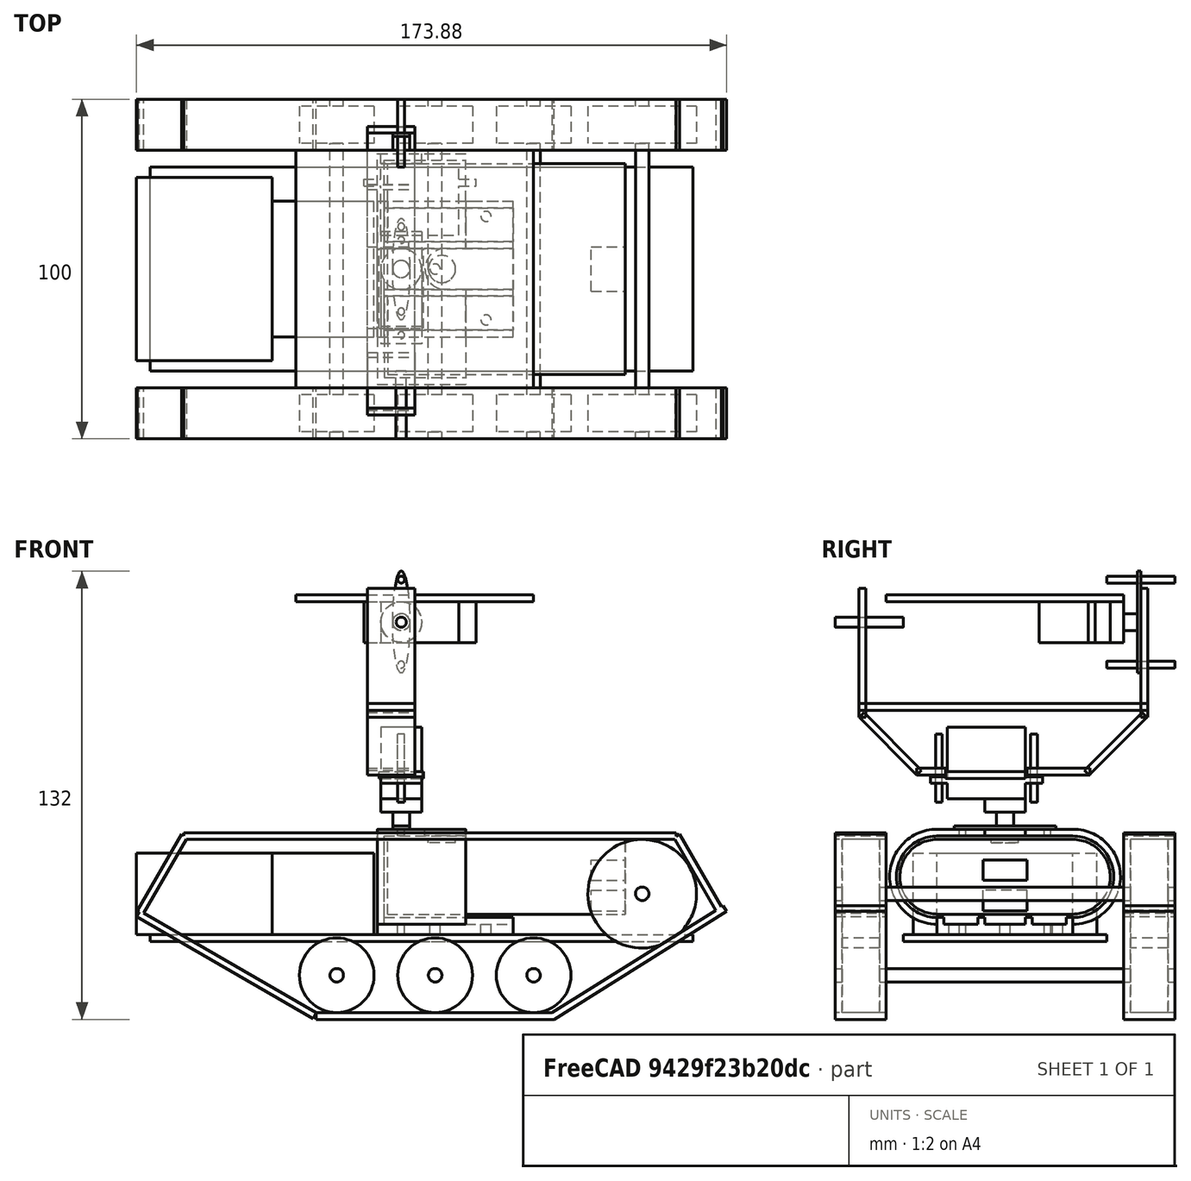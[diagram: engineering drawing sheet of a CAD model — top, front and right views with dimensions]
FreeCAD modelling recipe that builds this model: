
FCSTD DOCUMENT
Label: androidtank_2
License: CC-BY 3.0
LicenseURL: http://creativecommons.org/licenses/by/3.0/
objects: Part::Box×32, Part::Cylinder×30, Part::MultiFuse×18, Part::Cut×3, Part::FeaturePython×2, App::DocumentObjectGroup×1
note: 85 computed .brp shape members not serialized (recipe doc carries the construction recipe); baked Part::Feature solids carry a one-line shape summary decoded from their .brp

FEATURE [Part::Box] Box  label="MainFrame"
  Height = 2
  Length = 160
  Width = 60
FEATURE [Part::Box] Box001001  label="Moter Unit2"
  Height = 24
  Length = 30
  Placement = pos=(36,10,2) rot=(0,0,1;0rad)
  Width = 40
FEATURE [Part::Cylinder] Cylinder002  label="Wheel1"
  Angle = 360
  Height = 11
  Placement = pos=(20,-7,14) rot=(1,0,0;1.5708rad)
  Radius = 16
FEATURE [Part::Cylinder] Cylinder  label="Shaft"
  Angle = 360
  Height = 100
  Placement = pos=(20,-20,14) rot=(-1,0,0;1.5708rad)
  Radius = 2
FEATURE [Part::Cylinder] Cylinder002001  label="Wheel2"
  Angle = 360
  Height = 11
  Placement = pos=(20,78,14) rot=(1,0,0;1.5708rad)
  Radius = 16
FEATURE [Part::MultiFuse] Fusion001  label="WheelSet2"
  Placement = pos=(125,0,0) rot=(0,0,1;0rad)
  Shapes = -> [Cylinder,Cylinder002,Cylinder002001]
FEATURE [Part::Box] Box001002
  Height = 2
  Length = 145
  Placement = pos=(10,-20,30) rot=(0,0,1;0rad)
  Width = 15
FEATURE [Part::Box] Box001002001
  Height = 2
  Length = 70
  Placement = pos=(49,-20,-23) rot=(0,0,1;0rad)
  Width = 15
FEATURE [Part::Box] Box001002001001
  Height = 2
  Length = 60
  Placement = pos=(119,-20,-23) rot=(0,-1,0;0.558505rad)
  Width = 15
FEATURE [Part::Box] Box001002001002
  Height = 2
  Length = 60
  Placement = pos=(49,-20,-21) rot=(0,1,0;3.66519rad)
  Width = 15
FEATURE [Part::Box] Box001002001003
  Height = 2
  Length = 26
  Placement = pos=(-2,-20,8) rot=(0,-1,0;1.0472rad)
  Width = 15
FEATURE [Part::Box] Box001002001003001
  Height = 2
  Length = 26
  Placement = pos=(169,-20,9) rot=(0,-1,0;2.0944rad)
  Width = 15
FEATURE [Part::MultiFuse] Fusion002001002  label="Caterpiller1"
  Shapes = -> [Box001002,Box001002001,Box001002001002,Box001002001001,Box001002001003,Box001002001003001]
FEATURE [Part::MultiFuse] Fusion002001002001  label="Caterpiller2"
  Placement = pos=(0,85,0) rot=(0,0,1;0rad)
  Shapes = -> [Box001002,Box001002001,Box001002001002,Box001002001001,Box001002001003,Box001002001003001]
FEATURE [Part::Cylinder] Cylinder002001001002  label="Wheel006"
  Angle = 360
  Height = 11
  Placement = pos=(20,78,14) rot=(1,0,0;1.5708rad)
  Radius = 11
FEATURE [Part::Cylinder] Cylinder002001001002001  label="Wheel007"
  Angle = 360
  Height = 11
  Placement = pos=(20,-7,14) rot=(1,0,0;1.5708rad)
  Radius = 11
FEATURE [Part::Cylinder] Cylinder002001002001  label="Shaft002"
  Angle = 360
  Height = 100
  Placement = pos=(20,-20,14) rot=(-1,0,0;1.5708rad)
  Radius = 2
FEATURE [Part::MultiFuse] Fusion002001002002002  label="SWheelSet1"
  Placement = pos=(35,0,-24) rot=(0,0,1;0rad)
  Shapes = -> [Cylinder002001002001,Cylinder002001001002,Cylinder002001001002001]
FEATURE [Part::MultiFuse] Fusion002001002002002001  label="SWheelSet2"
  Placement = pos=(64,0,-24) rot=(0,0,1;0rad)
  Shapes = -> [Cylinder002001002001,Cylinder002001001002,Cylinder002001001002001]
FEATURE [Part::MultiFuse] Fusion002001002002002001001  label="SWheelSet3"
  Placement = pos=(93,0,-24) rot=(0,0,1;0rad)
  Shapes = -> [Cylinder002001002001,Cylinder002001001002,Cylinder002001001002001]
FEATURE [Part::Box] Box001002001003002
  Height = 22
  Length = 70
  Placement = pos=(0,0,-11) rot=(0,0,1;0rad)
  Width = 40
FEATURE [Part::Cylinder] Cylinder002001001002002
  Angle = 360
  Height = 70
  Placement = pos=(0,0,0) rot=(0,1,0;1.5708rad)
  Radius = 11
FEATURE [Part::Cylinder] Cylinder001
  Angle = 360
  Height = 70
  Placement = pos=(0,40,0) rot=(0,1,0;1.5708rad)
  Radius = 11
FEATURE [Part::Cylinder] Cylinder002001001002003  label="PowerButton"
  Angle = 360
  Height = 2
  Placement = pos=(16,20,10) rot=(0,0,1;0rad)
  Radius = 4
FEATURE [Part::Box] Box001002001003003  label="USB1"
  Height = 6
  Length = 15
  Placement = pos=(60,13.5,-1) rot=(0,0,1;0rad)
  Width = 13
FEATURE [Part::Box] Box001001001  label="USB2"
  Height = 6
  Length = 15
  Placement = pos=(60,13.5,-10) rot=(0,0,1;0rad)
  Width = 13
FEATURE [Part::MultiFuse] Fusion002001002002002001002
  Shapes = -> [Cylinder001,Box001002001003002,Cylinder002001001002002]
FEATURE [Part::MultiFuse] Fusion001001
  Shapes = -> [Box001001001,Cylinder002001001002003,Box001002001003003]
FEATURE [Part::Cut] Cut  label="Eneloop"
  Base = -> Fusion002001002002002001002
  Placement = pos=(70,10,19) rot=(0,0,1;0rad)
  Tool = -> Fusion001001
FEATURE [Part::Cylinder] Cylinder001001  label="Cylinder002"
  Angle = 360
  Height = 26
  Placement = pos=(0,50,19) rot=(0,1,0;1.5708rad)
  Radius = 14
FEATURE [Part::Box] Box001002001003002001  label="Box002"
  Height = 28
  Length = 26
  Placement = pos=(0,10,5) rot=(0,0,1;0rad)
  Width = 40
FEATURE [Part::Cylinder] Cylinder002001001002002001  label="Cylinder003"
  Angle = 360
  Height = 26
  Placement = pos=(0,10,19) rot=(0,1,0;1.5708rad)
  Radius = 14
FEATURE [Part::Box] Box001  label="Moter Unit1"
  Height = 24
  Length = 40
  Placement = pos=(-4,3,2) rot=(0,0,1;0rad)
  Width = 54
FEATURE [App::DocumentObjectGroup] ____________  label="DriveFrame"
  Group = -> [Box,Box001,Box001001,Fusion002001002,Fusion002001002001,Fusion002001002002002,Fusion002001002002002001,Fusion002001002002002001001,Fusion001]
FEATURE [Part::Box] Box001002001003002001001  label="Box003"
  Height = 5
  Length = 40
  Placement = pos=(0,10,2) rot=(0,0,1;0rad)
  Width = 40
FEATURE [Part::Box] Box001002001003002001002  label="Box004"
  Height = 24
  Length = 26
  Placement = pos=(2,10,7) rot=(0,0,1;0rad)
  Width = 40
FEATURE [Part::Cylinder] Cylinder001001001  label="Cylinder004"
  Angle = 360
  Height = 26
  Placement = pos=(2,50,19) rot=(0,1,0;1.5708rad)
  Radius = 12
FEATURE [Part::Cylinder] Cylinder002001001002002001001  label="Cylinder005"
  Angle = 360
  Height = 26
  Placement = pos=(2,10,19) rot=(0,1,0;1.5708rad)
  Radius = 12
FEATURE [Part::Cylinder] Cylinder002001001002003001  label="PowerButton001"
  Angle = 360
  Height = 4
  Placement = pos=(20,30,30) rot=(0,0,1;0rad)
  Radius = 6
FEATURE [Part::Box] Box001002001003002001003  label="Box005"
  Height = 4
  Length = 10
  Placement = pos=(20,24,30) rot=(0,0,1;0rad)
  Width = 12
FEATURE [Part::Box] Box001002001003002001001001  label="Box006"
  Height = 3
  Length = 40
  Placement = pos=(2,12,5) rot=(0,0,1;0rad)
  Width = 10
FEATURE [Part::Box] Box001002001003002001001001001  label="Box007"
  Height = 3
  Length = 40
  Placement = pos=(2,24,5) rot=(0,0,1;0rad)
  Width = 12
FEATURE [Part::Box] Box001002001003002001001001001001  label="Box008"
  Height = 3
  Length = 40
  Placement = pos=(2,38,5) rot=(0,0,1;0rad)
  Width = 10
FEATURE [Part::MultiFuse] Fusion002001002002002001003
  Shapes = -> [Box001002001003002001,Cylinder001001,Cylinder002001001002002001,Box001002001003002001001]
FEATURE [Part::MultiFuse] Fusion002001002002002001004
  Shapes = -> [Box001002001003002001002,Cylinder002001001002002001001,Cylinder001001001,Box001002001003002001001001001001,Box001002001003002001001001001,Box001002001003002001001001,Box001002001003002001003,Cylinder002001001002003001]
FEATURE [Part::Cut] Cut001  label="BatteryFrame"
  Base = -> Fusion002001002002002001003
  Placement = pos=(67,0,0) rot=(0,0,1;0rad)
  Tool = -> Fusion002001002002002001004
FEATURE [Part::Cylinder] Cylinder002001001002002001002001  label="Cylinder007"
  Angle = 360
  Height = 40
  Placement = pos=(74,17.5,0) rot=(0,0,1;0rad)
  Radius = 1
FEATURE [Part::Cylinder] Cylinder002001001002002001002  label="Cylinder006"
  Angle = 360
  Height = 40
  Placement = pos=(74,42.5,0) rot=(0,0,1;0rad)
  Radius = 1
FEATURE [Part::Cylinder] Cylinder002001001002002001002001001  label="Cylinder008"
  Angle = 360
  Height = 40
  Placement = pos=(84,30,0) rot=(0,0,1;0rad)
  Radius = 1.5
FEATURE [Part::Cylinder] Cylinder002001001002002001002001002  label="Cylinder009"
  Angle = 360
  Height = 40
  Placement = pos=(99,45.5,0) rot=(0,0,1;0rad)
  Radius = 1.5
FEATURE [Part::Cylinder] Cylinder002001001002002001002001003  label="Cylinder0010"
  Angle = 360
  Height = 40
  Placement = pos=(99,15,0) rot=(0,0,1;0rad)
  Radius = 1.5
FEATURE [Part::MultiFuse] Fusion002001002002002001005  label="BatteryFrameHoles"
  Shapes = -> [Cylinder002001001002002001002001,Cylinder002001001002002001002,Cylinder002001001002002001002001003,Cylinder002001001002002001002001002,Cylinder002001001002002001002001001]
FEATURE [Part::Cut] Cut002  label="BatteryFrame2"
  Base = -> Cut001
  Tool = -> Fusion002001002002002001005
FEATURE [Part::Box] Box001002001003002001001001001002  label="ServoBody"
  Height = 21
  Length = 23
  Width = 12
FEATURE [Part::Cylinder] Cylinder002001001002002001002001004  label="ServoBody2"
  Angle = 360
  Height = 4
  Placement = pos=(6,6,21) rot=(0,0,1;0rad)
  Radius = 6
FEATURE [Part::Box] Box001002001003002001001001001003  label="ServoBody3"
  Height = 2
  Length = 33
  Placement = pos=(-5,0,14.5) rot=(0,0,1;0rad)
  Width = 12
FEATURE [Part::Cylinder] Cylinder001001002  label="ServoAxis"
  Angle = 360
  Height = 4
  Placement = pos=(6,6,24) rot=(0,0,1;0rad)
  Radius = 2.5
FEATURE [Part::MultiFuse] Fusion005  label="ServoArmL"
  Shapes = -> [Cylinder001001002,Box001002001003002001001001001003,Box001002001003002001001001001002,Cylinder002001001002002001002001004]
FEATURE [Part::Cylinder] Cylinder002001001002002001002001005
  Angle = 360
  Height = 2
  Radius = 2.5
FEATURE [Part::FeaturePython] Scale  # Draft clone (typed FeaturePython)
  Objects = -> [Cylinder002001001002002001002001005]
  Placement = pos=(0,0,1) rot=(0,0,1;0rad)
  Scale = (6,1,0.5)
FEATURE [Part::MultiFuse] Fusion  label="Arm"
  Placement = pos=(6,6,28) rot=(0,0,1;0rad)
  Shapes = -> [Cylinder002001001002002001002001005,Scale]
FEATURE [Part::MultiFuse] Fusion006  label="ServoYaw"
  Placement = pos=(80,36,63) rot=(0.707107,-0.707107,0;3.14159rad)
  Shapes = -> [Fusion005,Fusion]
FEATURE [Part::Box] Box001002001003002001001001001004  label="ServoBody004"
  Height = 21
  Length = 23
  Width = 12
FEATURE [Part::Cylinder] Cylinder002001001002002001002001006  label="ServoBody005"
  Angle = 360
  Height = 4
  Placement = pos=(6,6,21) rot=(0,0,1;0rad)
  Radius = 6
FEATURE [Part::Box] Box001002001003002001001001001005  label="ServoBody006"
  Height = 2
  Length = 33
  Placement = pos=(-5,0,14.5) rot=(0,0,1;0rad)
  Width = 12
FEATURE [Part::Cylinder] Cylinder001001003  label="ServoAxis001"
  Angle = 360
  Height = 4
  Placement = pos=(6,6,24) rot=(0,0,1;0rad)
  Radius = 2.5
FEATURE [Part::MultiFuse] Fusion005001  label="ServoArmL001"
  Shapes = -> [Cylinder001001003,Box001002001003002001001001001005,Box001002001003002001001001001004,Cylinder002001001002002001002001006]
FEATURE [Part::Cylinder] Cylinder002001001002002001002001007
  Angle = 360
  Height = 2
  Radius = 2.5
FEATURE [Part::FeaturePython] Scale001  # Draft clone (typed FeaturePython)
  Objects = -> [Cylinder002001001002002001002001007]
  Placement = pos=(0,0,1) rot=(0,0,1;0rad)
  Scale = (6,1,0.5)
FEATURE [Part::MultiFuse] Fusion002001002002002001006  label="Arm001"
  Placement = pos=(6,6,28) rot=(0,0,1;1.5708rad)
  Shapes = -> [Cylinder002001001002002001002001007,Scale001]
FEATURE [Part::MultiFuse] Fusion006001  label="ServoPitch"
  Placement = pos=(68,40,100) rot=(-1,0,0;1.57079rad)
  Shapes = -> [Fusion005001,Fusion002001002002002001006]
FEATURE [Part::Box] Box001002001003002001001001001006  label="Box009"
  Height = 2
  Length = 70
  Placement = pos=(43,-5,100) rot=(0,0,1;0rad)
  Width = 70
FEATURE [Part::Box] Box001002001003002001001001001006001  label="Box010"
  Height = 38
  Length = 14
  Placement = pos=(64,70,66) rot=(0,0,1;0rad)
  Width = 2
FEATURE [Part::Box] Box001002001003002001001001001006001001  label="Box011"
  Height = 2
  Length = 13
  Placement = pos=(67.5,12.5,48) rot=(0,0,1;0rad)
  Width = 23.5
FEATURE [Part::Box] Box001002001003002001001001001006001001001  label="Box012"
  Height = 38
  Length = 14
  Placement = pos=(64,-13,66) rot=(0,0,1;0rad)
  Width = 2
FEATURE [Part::Cylinder] Cylinder002001001002002001002001008  label="Hole1"
  Angle = 360
  Height = 20
  Placement = pos=(74,-20,94) rot=(-1,0,0;1.5708rad)
  Radius = 1.5
FEATURE [Part::Cylinder] Cylinder002001001002002001002001008001  label="Hole2"
  Angle = 360
  Height = 20
  Placement = pos=(74,60,106.5) rot=(-1,0,0;1.5708rad)
  Radius = 1
FEATURE [Part::Cylinder] Cylinder002001001002002001002001008001001  label="Hole4"
  Angle = 360
  Height = 20
  Placement = pos=(74,38.5,41) rot=(0,0,1;0rad)
  Radius = 1
FEATURE [Part::Cylinder] Cylinder002001001002002001002001008001001001  label="Hole3"
  Angle = 360
  Height = 20
  Placement = pos=(74,60,81.5) rot=(-1,0,0;1.5708rad)
  Radius = 1
FEATURE [Part::Cylinder] Cylinder002001001002002001002001008001001002  label="Hole5"
  Angle = 360
  Height = 20
  Placement = pos=(74,10.5,41) rot=(0,0,1;0rad)
  Radius = 1
FEATURE [Part::Box] Box001002001003002001001001001006001001001001  label="Box013"
  Height = 24
  Length = 14
  Placement = pos=(64,4,49) rot=(1,0,0;0.785397rad)
  Width = 2
FEATURE [Part::Box] Box001002001003002001001001001006001001001001001  label="Box014"
  Height = 24
  Length = 14
  Placement = pos=(64,53.41,50.41) rot=(-1,0,0;0.785397rad)
  Width = 2
FEATURE [Part::MultiFuse] Fusion002001002002002001008
  Shapes = -> [Cylinder002001001002002001002001008001,Cylinder002001001002002001002001008001001001,Cylinder002001001002002001002001008,Cylinder002001001002002001002001008001001002,Cylinder002001001002002001002001008001001,Box001002001003002001001001001006001001]
FEATURE [Part::Box] Box001002001003002001001001001006001001002001  label="Box016"
  Height = 2
  Length = 14
  Placement = pos=(64,4,49) rot=(0,0,1;0rad)
  Width = 8.5
FEATURE [Part::Box] Box001002001003002001001001001006001001002001001  label="Box017"
  Height = 2
  Length = 14
  Placement = pos=(64,36.5,49) rot=(0,0,1;0rad)
  Width = 18.5
FEATURE [Part::Box] Box001002001003002001001001001006001001002001002  label="Box015"
  Height = 2
  Length = 14
  Placement = pos=(64,-13,68) rot=(0,0,1;0rad)
  Width = 85
